FCSTD DOCUMENT  (FreeCAD 0.19R24291 (Git))
Label: 1U_erratic_radio_box_base
License: All rights reserved
LicenseURL: http://en.wikipedia.org/wiki/All_rights_reserved
objects: Part::Feature×29, App::Part×17, Sketcher::SketchObject×5, PartDesign::Pad×4, PartDesign::Body×2, Mesh::Feature×1, PartDesign::Pocket×1
note: 46 computed .brp shape members not serialized (recipe doc carries the construction recipe); baked Part::Feature solids carry a one-line shape summary decoded from their .brp

FEATURE [Sketcher::SketchObject] Sketch
  FullyConstrained = true
  MapMode = 5
  Support = -> [XY_Plane]
  sketch-geometry (44):
    g0: LineSegment StartX=200 StartY=123 StartZ=0 EndX=200 EndY=-123 EndZ=0
    g1: LineSegment StartX=200 StartY=-123 StartZ=0 EndX=-200 EndY=-123 EndZ=0
    g2: LineSegment StartX=-200 StartY=-123 StartZ=0 EndX=-200 EndY=123 EndZ=0
    g3: LineSegment StartX=200 StartY=-123 StartZ=0 EndX=200 EndY=-87 EndZ=0
    g4: LineSegment StartX=200 StartY=-87 StartZ=0 EndX=190 EndY=-87 EndZ=0
    g5: LineSegment StartX=190 StartY=-87 StartZ=0 EndX=190 EndY=-71 EndZ=0
    g6: LineSegment StartX=190 StartY=-71 StartZ=0 EndX=200 EndY=-71 EndZ=0
    g7: LineSegment StartX=200 StartY=-71 StartZ=0 EndX=200 EndY=0 EndZ=0
    g8: LineSegment StartX=-200 StartY=-123 StartZ=0 EndX=-200 EndY=-87 EndZ=0
    g9: LineSegment StartX=-200 StartY=-87 StartZ=0 EndX=-190 EndY=-87 EndZ=0
    g10: LineSegment StartX=-190 StartY=-87 StartZ=0 EndX=-190 EndY=-71 EndZ=0
    g11: LineSegment StartX=-190 StartY=-71 StartZ=0 EndX=-200 EndY=-71 EndZ=0
    g12: LineSegment StartX=-200 StartY=-71 StartZ=0 EndX=-200 EndY=0 EndZ=0
    g13: LineSegment StartX=-200 StartY=123 StartZ=0 EndX=-200 EndY=87 EndZ=0
    g14: LineSegment StartX=-200 StartY=87 StartZ=0 EndX=-190 EndY=87 EndZ=0
    g15: LineSegment StartX=-190 StartY=87 StartZ=0 EndX=-190 EndY=71 EndZ=0
    g16: LineSegment StartX=-190 StartY=71 StartZ=0 EndX=-200 EndY=71 EndZ=0
    g17: LineSegment StartX=-200 StartY=71 StartZ=0 EndX=-200 EndY=0 EndZ=0
    g18: LineSegment StartX=200 StartY=123 StartZ=0 EndX=200 EndY=87 EndZ=0
    g19: LineSegment StartX=200 StartY=87 StartZ=0 EndX=190 EndY=87 EndZ=0
    g20: LineSegment StartX=190 StartY=87 StartZ=0 EndX=190 EndY=71 EndZ=0
    g21: LineSegment StartX=190 StartY=71 StartZ=0 EndX=200 EndY=71 EndZ=0
    g22: LineSegment StartX=200 StartY=71 StartZ=0 EndX=200 EndY=0 EndZ=0
    g23: GeomPoint X=-160 Y=123 Z=0
    g24: GeomPoint X=0 Y=123 Z=0
    g25: GeomPoint X=160 Y=123 Z=0
    g26: LineSegment StartX=-160 StartY=123 StartZ=0 EndX=0 EndY=123 EndZ=0
    g27: LineSegment StartX=160 StartY=123 StartZ=0 EndX=0 EndY=123 EndZ=0
    g28: LineSegment StartX=-200 StartY=123 StartZ=0 EndX=-168 EndY=123 EndZ=0
    g29: LineSegment StartX=-168 StartY=123 StartZ=0 EndX=-168 EndY=113 EndZ=0
    g30: LineSegment StartX=-168 StartY=113 StartZ=0 EndX=-152 EndY=113 EndZ=0
    g31: LineSegment StartX=-152 StartY=113 StartZ=0 EndX=-152 EndY=123 EndZ=0
    g32: LineSegment StartX=-152 StartY=123 StartZ=0 EndX=-8 EndY=123 EndZ=0
    g33: LineSegment StartX=-8 StartY=123 StartZ=0 EndX=-8 EndY=113 EndZ=0
    g34: LineSegment StartX=-8 StartY=113 StartZ=0 EndX=8 EndY=113 EndZ=0
    g35: LineSegment StartX=8 StartY=113 StartZ=0 EndX=8 EndY=123 EndZ=0
    g36: LineSegment StartX=8 StartY=123 StartZ=0 EndX=152 EndY=123 EndZ=0
    g37: LineSegment StartX=152 StartY=123 StartZ=0 EndX=152 EndY=113 EndZ=0
    g38: LineSegment StartX=152 StartY=113 StartZ=0 EndX=168 EndY=113 EndZ=0
    g39: LineSegment StartX=168 StartY=113 StartZ=0 EndX=168 EndY=123 EndZ=0
    g40: LineSegment StartX=168 StartY=123 StartZ=0 EndX=200 EndY=123 EndZ=0
    g41: GeomPoint X=160 Y=113 Z=0
    g42: GeomPoint X=0 Y=113 Z=0
    g43: GeomPoint X=-160 Y=113 Z=0
  constraints (118):
    c: Coincident(g0,g1)
    c: Coincident(g1,g2)
    c: Horizontal(g1)
    c: Vertical(g0)
    c: Vertical(g2)
    c: Symmetric(g0,g1,g-1)
    c: DistanceX(g1,g1) = 400
    c: DistanceY(g0,g0) = 246
    c: Coincident(g3,g1)
    c: PointOnObject(g3,g0)
    c: Coincident(g4,g3)
    c: Horizontal(g4)
    c: Coincident(g5,g4)
    c: Vertical(g5)
    c: Coincident(g6,g5)
    c: PointOnObject(g6,g0)
    c: Horizontal(g6)
    c: Coincident(g7,g6)
    c: PointOnObject(g7,g0)
    c: PointOnObject(g7,g-1)
    c: DistanceY(g1,g3) = 36
    c: DistanceY(g1,g6) = 52
    c: DistanceX(g4,g4) = 10
    c: Coincident(g9,g8)
    c: Horizontal(g9)
    c: Coincident(g10,g9)
    c: Vertical(g10)
    c: Coincident(g11,g10)
    c: Horizontal(g11)
    c: Coincident(g12,g11)
    c: Coincident(g19,g18)
    c: Horizontal(g19)
    c: Coincident(g20,g19)
    c: Vertical(g20)
    c: Coincident(g21,g20)
    c: Horizontal(g21)
    c: Coincident(g22,g21)
    c: Coincident(g14,g13)
    c: Horizontal(g14)
    c: Coincident(g15,g14)
    c: Vertical(g15)
    c: Coincident(g16,g15)
    c: Horizontal(g16)
    c: Coincident(g17,g16)
    c: Equal(g5,g20)
    c: Equal(g20,g15)
    c: Equal(g15,g10)
    c: Equal(g21,g4)
    c: Equal(g4,g9)
    c: Equal(g9,g16)
    c: Equal(g3,g8)
    c: Equal(g8,g13)
    c: Equal(g13,g18)
    c: Coincident(g12,g17)
    c: PointOnObject(g12,g-1)
    c: PointOnObject(g12,g2)
    c: Vertical(g12)
    c: Coincident(g8,g1)
    c: Vertical(g8)
    c: Vertical(g17)
    c: Vertical(g13)
    c: Vertical(g22)
    c: Coincident(g7,g22)
    c: Vertical(g18)
    c: PointOnObject(g24,g-2)
    c: DistanceX(g24,g25) = 160
    c: Coincident(g26,g23)
    c: Coincident(g26,g24)
    c: Coincident(g27,g25)
    c: Coincident(g27,g24)
    c: Horizontal(g24,g18)
    c: Equal(g27,g26)
    c: Horizontal(g27)
    c: Horizontal(g26)
    c: Horizontal(g2,g18)
    c: Coincident(g13,g2)
    c: Coincident(g18,g0)
    c: Coincident(g13,g28)
    c: Horizontal(g28)
    c: Coincident(g28,g29)
    c: Vertical(g29)
    c: Coincident(g29,g30)
    c: Horizontal(g30)
    c: Coincident(g30,g31)
    c: PointOnObject(g31,g26)
    c: Vertical(g31)
    c: Horizontal(g32)
    c: Coincident(g32,g33)
    c: Vertical(g33)
    c: Coincident(g33,g34)
    c: Horizontal(g34)
    c: Coincident(g34,g35)
    c: PointOnObject(g35,g27)
    c: Vertical(g35)
    c: Coincident(g35,g36)
    c: PointOnObject(g36,g27)
    c: Coincident(g36,g37)
    c: Coincident(g37,g38)
    c: Horizontal(g38)
    c: Coincident(g38,g39)
    c: Vertical(g39)
    c: Coincident(g39,g40)
    c: Coincident(g40,g18)
    c: Vertical(g37)
    c: Equal(g38,g34)
    c: Equal(g34,g30)
    c: Equal(g30,g5)
    c: Horizontal(g40)
    c: Equal(g31,g35)
    c: Equal(g35,g39)
    c: Equal(g39,g21)
    c: Symmetric(g38,g37,g41)
    c: Vertical(g41,g25)
    c: Symmetric(g34,g33,g42)
    c: Vertical(g42,g24)
    c: Symmetric(g30,g29,g43)
    c: Vertical(g43,g23)
    c: Coincident(g32,g31)
FEATURE [PartDesign::Pad] Pad
  Direction = (1,1,1)
  Length = 5
  Length2 = 100
  Profile = -> Sketch
  Type = 0
FEATURE [Part::Feature] Part__Feature  label="p2"
  Placement = pos=(0,0,0.5) rot=(0,0,1;0rad)
  shape: bbox 62.5 x 51.1 x 28 mm, 628 faces (baked)
FEATURE [Part::Feature] Part__Feature001  label="PCB"
  Placement = pos=(-7.1e-15,0.2,0) rot=(0,0,1;0rad)
  shape: bbox 73.06 x 49 x 22.6 mm, 145 faces (baked)
FEATURE [App::Part] RS_15  label="RS-15 A"
  Group = -> [Part__Feature,Part__Feature001]
  Origin = -> Origin002
  Placement = pos=(-80,-61,34) rot=(0,0,1;1.5708rad)
FEATURE [Part::Feature] Part__Feature002  label="Raspberry Pi 3 Light Version"
  Placement = pos=(-103,69,11) rot=(0,0,1;0rad)
  shape: bbox 89.96 x 57.63 x 18.91 mm, 9075 faces, 217 solids (baked)
FEATURE [App::Part] Part001  label="RaspberryPi"
  Group = -> [Part__Feature002]
  Origin = -> Origin003
  Placement = pos=(5,9,0) rot=(0,0,1;0rad)
FEATURE [Part::Feature] Part__Feature003  label="PCB001"
  Placement = pos=(-7.1e-15,0.2,0) rot=(0,0,1;0rad)
  shape: bbox 73.06 x 49 x 22.6 mm, 145 faces (baked)
FEATURE [Part::Feature] Part__Feature004  label="p003"
  Placement = pos=(0,0,0.5) rot=(0,0,1;0rad)
  shape: bbox 62.5 x 51.1 x 28 mm, 628 faces (baked)
FEATURE [App::Part] RS_016  label="RS-15 B"
  Group = -> [Part__Feature004,Part__Feature003]
  Origin = -> Origin004
  Placement = pos=(-19,-61,34) rot=(0,0,1;1.5708rad)
FEATURE [Part::Feature] Part__Feature005  label="Pcb"
  Placement = pos=(-142.73,80.22,0) rot=(0,0,1;0rad)
  shape: bbox 55.31 x 70 x 1.6 mm, 52 faces (baked)
FEATURE [Part::Feature] Part__Feature006  label="PCB_Sketch"
  shape: bbox 55.31 x 70 x 2e-07 mm, 0 faces, 0 solids (baked)
FEATURE [App::Part] Board_Geoms
  Group = -> [Part__Feature005,Part__Feature006]
  Origin = -> Origin006
FEATURE [Part::Feature] Part__Feature007  label="C22_CP_Elec_5x53_58AF1F3F"
  Placement = pos=(-2.94,-32.29,0) rot=(0,0,1;3.14159rad)
  shape: bbox 6.985 x 6.828 x 5.3 mm, 41 faces (baked)
FEATURE [Part::Feature] Part__Feature008  label="C23_CP_Elec_5x53_58AF1F4D"
  Placement = pos=(-2.6,-14.04,0) rot=(0,0,1;3.14159rad)
  shape: bbox 6.985 x 6.828 x 5.3 mm, 41 faces (baked)
FEATURE [Part::Feature] Part__Feature009  label="C24_CP_Elec_5x53_58AF1F5B"
  Placement = pos=(-2.79,3.79,0) rot=(0,0,1;3.14159rad)
  shape: bbox 6.985 x 6.828 x 5.3 mm, 41 faces (baked)
FEATURE [Part::Feature] Part__Feature010  label="J1_676430910_58AF1F9A"
  Placement = pos=(2.25,-26.25,0) rot=(0.57735,0.57735,0.57735;2.0944rad)
  shape: bbox 15.26 x 16.01 x 11.45 mm, 499 faces (baked)
FEATURE [Part::Feature] Part__Feature011  label="J2_676430910_58AF1FA7"
  Placement = pos=(2.25,-8.15,0) rot=(0.57735,0.57735,0.57735;2.0944rad)
  shape: bbox 15.26 x 16.01 x 11.45 mm, 499 faces (baked)
FEATURE [Part::Feature] Part__Feature012  label="J3_676430910_58AF1FB4[2]"
  Placement = pos=(2.25,9.84,0) rot=(0.57735,0.57735,0.57735;2.0944rad)
  shape: bbox 15.26 x 16.01 x 11.45 mm, 499 faces (baked)
FEATURE [Part::Feature] Part__Feature013  label="P1_USB_Micro-B_Molex_47346-0001_58AF1FC6"
  Placement = pos=(-36.58,18.53,0) rot=(0,0,-1;1.5708rad)
  shape: bbox 5.418 x 7.977 x 2.937 mm, 484 faces (baked)
FEATURE [Part::Feature] Part__Feature014  label="P5_USB_Mini-B_Lumberg_2486_01_Horizontal_58AF1FEC"
  Placement = pos=(-34.75,-26.5,0) rot=(0,0,-1;1.5708rad)
  shape: bbox 9.2 x 9.9 x 4.997 mm, 472 faces (baked)
FEATURE [App::Part] Top
  Group = -> [Part__Feature007,Part__Feature008,Part__Feature009,Part__Feature010,Part__Feature011,Part__Feature012,Part__Feature013,Part__Feature014]
  Origin = -> Origin007
FEATURE [App::Part] Step_Models
  Group = -> [Top]
  Origin = -> Origin008
FEATURE [App::Part] YKUSH  label="YKUSH_A"
  Group = -> [Board_Geoms,Step_Models]
  Origin = -> Origin009
  Placement = pos=(0,-69,10) rot=(0,0,1;0rad)
FEATURE [App::Part] Part003  label="SMPS"
  Group = -> [RS_016,RS_15]
  Origin = -> Origin010
  Placement = pos=(-1,-8,0) rot=(0,0,1;0rad)
FEATURE [Part::Feature] Part__Feature015  label="C23_CP_Elec_5x53_58AF1F4D001"
  Placement = pos=(-2.6,-14.04,0) rot=(0,0,1;3.14159rad)
  shape: bbox 6.985 x 6.828 x 5.3 mm, 41 faces (baked)
FEATURE [Part::Feature] Part__Feature016  label="J1_676430910_58AF1F9A001"
  Placement = pos=(2.25,-26.25,0) rot=(0.57735,0.57735,0.57735;2.0944rad)
  shape: bbox 15.26 x 16.01 x 11.45 mm, 499 faces (baked)
FEATURE [Part::Feature] Part__Feature017  label="Pcb001"
  Placement = pos=(-142.73,80.22,0) rot=(0,0,1;0rad)
  shape: bbox 55.31 x 70 x 1.6 mm, 52 faces (baked)
FEATURE [Part::Feature] Part__Feature018  label="C24_CP_Elec_5x53_58AF1F5B001"
  Placement = pos=(-2.79,3.79,0) rot=(0,0,1;3.14159rad)
  shape: bbox 6.985 x 6.828 x 5.3 mm, 41 faces (baked)
FEATURE [Part::Feature] Part__Feature019  label="J2_676430910_58AF1FA008"
  Placement = pos=(2.25,-8.15,0) rot=(0.57735,0.57735,0.57735;2.0944rad)
  shape: bbox 15.26 x 16.01 x 11.45 mm, 499 faces (baked)
FEATURE [Part::Feature] Part__Feature020  label="J3_676430910_58AF1FB4[2]001"
  Placement = pos=(2.25,9.84,0) rot=(0.57735,0.57735,0.57735;2.0944rad)
  shape: bbox 15.26 x 16.01 x 11.45 mm, 499 faces (baked)
FEATURE [Part::Feature] Part__Feature021  label="PCB_Sketch001"
  shape: bbox 55.31 x 70 x 2e-07 mm, 0 faces, 0 solids (baked)
FEATURE [App::Part] Board_Geoms001
  Group = -> [Part__Feature017,Part__Feature021]
  Origin = -> Origin012
FEATURE [Part::Feature] Part__Feature022  label="P1_USB_Micro-B_Molex_47346-0001_58AF1FC007"
  Placement = pos=(-36.58,18.53,0) rot=(0,0,-1;1.5708rad)
  shape: bbox 5.418 x 7.977 x 2.937 mm, 484 faces (baked)
FEATURE [Part::Feature] Part__Feature023  label="P5_USB_Mini-B_Lumberg_2486_01_Horizontal_58AF1FEC001"
  Placement = pos=(-34.75,-26.5,0) rot=(0,0,-1;1.5708rad)
  shape: bbox 9.2 x 9.9 x 4.997 mm, 472 faces (baked)
FEATURE [Part::Feature] Part__Feature024  label="C22_CP_Elec_5x53_58AF1F3F001"
  Placement = pos=(-2.94,-32.29,0) rot=(0,0,1;3.14159rad)
  shape: bbox 6.985 x 6.828 x 5.3 mm, 41 faces (baked)
FEATURE [App::Part] Top001
  Group = -> [Part__Feature024,Part__Feature015,Part__Feature018,Part__Feature016,Part__Feature019,Part__Feature020,Part__Feature022,Part__Feature023]
  Origin = -> Origin011
FEATURE [App::Part] Step_Models001
  Group = -> [Top001]
  Origin = -> Origin013
FEATURE [App::Part] YKUSH001  label="YKUSH_B"
  Group = -> [Board_Geoms001,Step_Models001]
  Origin = -> Origin014
  Placement = pos=(0,-69,24) rot=(0,0,1;0rad)
FEATURE [App::Part] Part002  label="Ykushes"
  Group = -> [YKUSH,YKUSH001]
  Origin = -> Origin005
  Placement = pos=(-0.6,4.5,0) rot=(0,0,1;0rad)
FEATURE [Mesh::Feature] HackRF_One
  Placement = pos=(164,105.3,8) rot=(0,0,1;3.14159rad)
FEATURE [Sketcher::SketchObject] Sketch001
  FullyConstrained = true
  MapMode = 5
  Support = -> [XY_Plane016]
  sketch-geometry (4):
    g0: LineSegment StartX=-26.5 StartY=20 StartZ=0 EndX=26.5 EndY=20 EndZ=0
    g1: LineSegment StartX=26.5 StartY=20 StartZ=0 EndX=26.5 EndY=-20 EndZ=0
    g2: LineSegment StartX=26.5 StartY=-20 StartZ=0 EndX=-26.5 EndY=-20 EndZ=0
    g3: LineSegment StartX=-26.5 StartY=-20 StartZ=0 EndX=-26.5 EndY=20 EndZ=0
  constraints (11):
    c: Coincident(g0,g1)
    c: Coincident(g1,g2)
    c: Coincident(g2,g3)
    c: Coincident(g3,g0)
    c: Horizontal(g0)
    c: Horizontal(g2)
    c: Vertical(g1)
    c: Vertical(g3)
    c: Symmetric(g0,g2,g-1)
    c: DistanceX(g2,g2) = 53
    c: DistanceY(g1,g1) = 40
FEATURE [PartDesign::Pad] Pad001
  Direction = (1,1,1)
  Length = 25
  Length2 = 100
  Profile = -> Sketch001
  Type = 0
FEATURE [Sketcher::SketchObject] Sketch002
  FullyConstrained = true
  MapMode = 5
  Placement = pos=(26.5,0,0) rot=(0.57735,0.57735,0.57735;2.0944rad)
  Support = -> [Pad001]
  sketch-geometry (1):
    g0: Circle CenterX=0 CenterY=13 CenterZ=0 NormalX=0 NormalY=0 NormalZ=1 AngleXU=0 Radius=5
  constraints (3):
    c: PointOnObject(g0,g-2)
    c: Diameter(g0) = 10
    c: DistanceY(g-1,g0) = 13
FEATURE [PartDesign::Pad] Pad002
  BaseFeature = -> Pad001
  Direction = (1,1,1)
  Length = 10
  Length2 = 100
  Profile = -> Sketch002
  Type = 0
FEATURE [Sketcher::SketchObject] Sketch003
  ExternalGeometry = -> [Pad002]
  FullyConstrained = true
  MapMode = 5
  Placement = pos=(-26.5,0,0) rot=(0.57735,-0.57735,-0.57735;2.0944rad)
  Support = -> [Pad002]
  sketch-geometry (6):
    g0: Circle CenterX=-5.5 CenterY=10 CenterZ=0 NormalX=0 NormalY=0 NormalZ=1 AngleXU=0 Radius=2.5
    g1: LineSegment StartX=-1.5 StartY=12.5 StartZ=0 EndX=9.5 EndY=12.5 EndZ=0
    g2: LineSegment StartX=9.5 StartY=12.5 StartZ=0 EndX=9.5 EndY=5.5 EndZ=0
    g3: LineSegment StartX=9.5 StartY=5.5 StartZ=0 EndX=-1.5 EndY=5.5 EndZ=0
    g4: LineSegment StartX=-1.5 StartY=5.5 StartZ=0 EndX=-1.5 EndY=12.5 EndZ=0
    g5: GeomPoint X=4 Y=9 Z=0
  constraints (16):
    c: Coincident(g1,g2)
    c: Coincident(g2,g3)
    c: Coincident(g3,g4)
    c: Coincident(g4,g1)
    c: Horizontal(g1)
    c: Horizontal(g3)
    c: Vertical(g2)
    c: Vertical(g4)
    c: Diameter(g0) = 5
    c: DistanceY(g-1,g0) = 10
    c: DistanceX(g-3,g0) = 14.5
    c: Symmetric(g1,g3,g5)
    c: DistanceY(g-1,g5) = 9
    c: DistanceY(g2,g2) = 7
    c: DistanceX(g1,g1) = 11
    c: DistanceX(g-3,g5) = 24
FEATURE [PartDesign::Pad] Pad003
  BaseFeature = -> Pad002
  Direction = (1,1,1)
  Length = 10
  Length2 = 100
  Profile = -> Sketch003
  Type = 0
FEATURE [PartDesign::Body] Body001
  Group = -> [Sketch001,Pad001,Sketch002,Pad002,Sketch003,Pad003]
  Origin = -> Origin016
  Placement = pos=(0,0,6) rot=(0,0,1;0rad)
  Tip = -> Pad003
FEATURE [App::Part] Part004  label="AIRSPY mock"
  Group = -> [Body001]
  Origin = -> Origin015
  Placement = pos=(15.5,-4,1.1) rot=(0,0,1;0rad)
FEATURE [Sketcher::SketchObject] Sketch004
  FullyConstrained = false
  MapMode = 5
  Placement = pos=(0,0,5) rot=(0,0,1;0rad)
  Support = -> [Pad]
  sketch-geometry (44):
    g0: LineSegment StartX=-180 StartY=105 StartZ=0 EndX=180 EndY=105 EndZ=0
    g1: LineSegment StartX=180 StartY=105 StartZ=0 EndX=180 EndY=-105 EndZ=0
    g2: LineSegment StartX=180 StartY=-105 StartZ=0 EndX=-180 EndY=-105 EndZ=0
    g3: LineSegment StartX=-180 StartY=-105 StartZ=0 EndX=-180 EndY=105 EndZ=0
    g4: Circle CenterX=-180 CenterY=105 CenterZ=0 NormalX=0 NormalY=0 NormalZ=1 AngleXU=0 Radius=1.6
    g5: Circle CenterX=-180 CenterY=-105 CenterZ=0 NormalX=0 NormalY=0 NormalZ=1 AngleXU=0 Radius=1.6
    g6: Circle CenterX=180 CenterY=-105 CenterZ=0 NormalX=0 NormalY=0 NormalZ=1 AngleXU=0 Radius=1.6
    g7: Circle CenterX=180 CenterY=105 CenterZ=0 NormalX=0 NormalY=0 NormalZ=1 AngleXU=0 Radius=1.6
    g8: Circle CenterX=-90 CenterY=-5 CenterZ=0 NormalX=0 NormalY=0 NormalZ=1 AngleXU=0 Radius=1.6
    g9: Circle CenterX=-90 CenterY=-44 CenterZ=0 NormalX=0 NormalY=0 NormalZ=1 AngleXU=0 Radius=1.6
    g10: Circle CenterX=-152 CenterY=-5 CenterZ=0 NormalX=0 NormalY=0 NormalZ=1 AngleXU=0 Radius=1.6
    g11: Circle CenterX=-152 CenterY=-44 CenterZ=0 NormalX=0 NormalY=0 NormalZ=1 AngleXU=0 Radius=1.6
    g12: LineSegment StartX=-90 StartY=-5 StartZ=0 EndX=-152 EndY=-5 EndZ=0
    g13: Circle CenterX=-90 CenterY=-15 CenterZ=0 NormalX=0 NormalY=0 NormalZ=1 AngleXU=0 Radius=1.6
    g14: Circle CenterX=-90 CenterY=-54 CenterZ=0 NormalX=0 NormalY=0 NormalZ=1 AngleXU=0 Radius=1.6
    g15: Circle CenterX=-152 CenterY=-15 CenterZ=0 NormalX=0 NormalY=0 NormalZ=1 AngleXU=0 Radius=1.6
    g16: Circle CenterX=-152 CenterY=-54 CenterZ=0 NormalX=0 NormalY=0 NormalZ=1 AngleXU=0 Radius=1.6
    g17: LineSegment StartX=-90 StartY=-15 StartZ=0 EndX=-152 EndY=-15 EndZ=0
    g18: LineSegment StartX=-90 StartY=-5 StartZ=0 EndX=-90 EndY=-15 EndZ=0
    g19: Circle CenterX=-90 CenterY=-25 CenterZ=0 NormalX=0 NormalY=0 NormalZ=1 AngleXU=0 Radius=1.6
    g20: Circle CenterX=-90 CenterY=-64 CenterZ=0 NormalX=0 NormalY=0 NormalZ=1 AngleXU=0 Radius=1.6
    g21: Circle CenterX=-152 CenterY=-25 CenterZ=0 NormalX=0 NormalY=0 NormalZ=1 AngleXU=0 Radius=1.6
    g22: Circle CenterX=-152 CenterY=-64 CenterZ=0 NormalX=0 NormalY=0 NormalZ=1 AngleXU=0 Radius=1.6
    g23: LineSegment StartX=-90 StartY=-25 StartZ=0 EndX=-152 EndY=-25 EndZ=0
    g24: LineSegment StartX=-90 StartY=-15 StartZ=0 EndX=-90 EndY=-25 EndZ=0
    g25: LineSegment StartX=-143 StartY=56 StartZ=0 EndX=-85 EndY=56 EndZ=0
    g26: LineSegment StartX=-85 StartY=56 StartZ=0 EndX=-85 EndY=105 EndZ=0
    g27: LineSegment StartX=-85 StartY=105 StartZ=0 EndX=-143 EndY=105 EndZ=0
    g28: LineSegment StartX=-143 StartY=105 StartZ=0 EndX=-143 EndY=56 EndZ=0
    g29: Circle CenterX=-143 CenterY=105 CenterZ=0 NormalX=0 NormalY=0 NormalZ=1 AngleXU=0 Radius=1.6
    g30: Circle CenterX=-143 CenterY=56 CenterZ=0 NormalX=0 NormalY=0 NormalZ=1 AngleXU=0 Radius=1.6
    g31: Circle CenterX=-85 CenterY=56 CenterZ=0 NormalX=0 NormalY=0 NormalZ=1 AngleXU=0 Radius=1.6
    g32: Circle CenterX=-85 CenterY=105 CenterZ=0 NormalX=0 NormalY=0 NormalZ=1 AngleXU=0 Radius=1.6
    g33: LineSegment StartX=-37.91 StartY=-38 StartZ=0 EndX=12 EndY=-38 EndZ=0
    g34: LineSegment StartX=12 StartY=-38 StartZ=0 EndX=12 EndY=-102.69 EndZ=0
    g35: LineSegment StartX=12 StartY=-102.69 StartZ=0 EndX=-37.91 EndY=-102.69 EndZ=0
    g36: LineSegment StartX=-37.91 StartY=-102.69 StartZ=0 EndX=-37.91 EndY=-38 EndZ=0
    g37: Circle CenterX=-37.91 CenterY=-38 CenterZ=0 NormalX=0 NormalY=0 NormalZ=1 AngleXU=0 Radius=1.6
    g38: Circle CenterX=12 CenterY=-38 CenterZ=0 NormalX=0 NormalY=0 NormalZ=1 AngleXU=0 Radius=1.6
    g39: Circle CenterX=-37.91 CenterY=-102.69 CenterZ=0 NormalX=0 NormalY=0 NormalZ=1 AngleXU=0 Radius=1.6
    g40: Circle CenterX=12 CenterY=-102.69 CenterZ=0 NormalX=0 NormalY=0 NormalZ=1 AngleXU=0 Radius=1.6
    g41: LineSegment StartX=-55 StartY=0 StartZ=0 EndX=55 EndY=0 EndZ=0
    g42: Circle CenterX=-55 CenterY=0 CenterZ=0 NormalX=0 NormalY=0 NormalZ=1 AngleXU=0 Radius=1.6
    g43: Circle CenterX=55 CenterY=0 CenterZ=0 NormalX=0 NormalY=0 NormalZ=1 AngleXU=0 Radius=1.6
  constraints (102):
    c: Coincident(g0,g1)
    c: Coincident(g1,g2)
    c: Coincident(g2,g3)
    c: Coincident(g3,g0)
    c: Horizontal(g0)
    c: Horizontal(g2)
    c: Vertical(g1)
    c: Vertical(g3)
    c: Symmetric(g0,g2,g-1)
    c: DistanceY(g1,g1) = 210
    c: DistanceX(g0,g0) = 360
    c: Coincident(g4,g0)
    c: Diameter(g4) = 3.2
    c: Equal(g4,g5) = 3.2
    c: Coincident(g5,g2)
    c: Equal(g4,g6) = 3.2
    c: Coincident(g6,g1)
    c: Equal(g4,g7) = 3.2
    c: Coincident(g7,g0)
    c: Equal(g4,g8) = 3.2
    c: Equal(g4,g9) = 3.2
    c: Vertical(g8,g9)
    c: DistanceY(g9,g8) = 39
    c: DistanceY(g8,g-1) = 5
    c: Vertical(g10,g11)
    c: DistanceY(g11,g10) = 39
    c: Coincident(g8,g12)
    c: Coincident(g10,g12)
    c: Horizontal(g12)
    c: DistanceX(g8,g-1) = 90
    c: DistanceX(g12,g12) = 62
    c: Vertical(g13,g14)
    c: DistanceY(g14,g13) = 39
    c: Vertical(g15,g16)
    c: DistanceY(g16,g15) = 39
    c: Coincident(g13,g17)
    c: Coincident(g15,g17)
    c: Horizontal(g17)
    c: Equal(g12,g17) = 62
    c: Coincident(g8,g18)
    c: Coincident(g13,g18)
    c: Distance(g18) = 10
    c: Vertical(g19,g20)
    c: DistanceY(g20,g19) = 39
    c: Vertical(g21,g22)
    c: DistanceY(g22,g21) = 39
    c: Coincident(g19,g23)
    c: Coincident(g21,g23)
    c: Horizontal(g23)
    c: Equal(g12,g23) = 62
    c: Coincident(g13,g24)
    c: Coincident(g19,g24)
    c: Equal(g18,g24)
    c: Parallel(g24,g18)
    c: Vertical(g18)
    c: Coincident(g25,g26)
    c: Coincident(g26,g27)
    c: Coincident(g27,g28)
    c: Coincident(g28,g25)
    c: Horizontal(g25)
    c: Horizontal(g27)
    c: Vertical(g26)
    c: Vertical(g28)
    c: DistanceX(g27,g27) = 58
    c: DistanceY(g28,g28) = 49
    c: DistanceX(g26,g-1) = 85
    c: DistanceY(g-1,g26) = 105
    c: Equal(g4,g29) = 3.2
    c: Coincident(g29,g27)
    c: Equal(g4,g30) = 3.2
    c: Coincident(g30,g25)
    c: Equal(g4,g31) = 3.2
    c: Coincident(g31,g25)
    c: Equal(g4,g32) = 3.2
    c: Coincident(g32,g26)
    c: Coincident(g33,g34)
    c: Coincident(g34,g35)
    c: Coincident(g35,g36)
    c: Coincident(g36,g33)
    c: Horizontal(g33)
    c: Horizontal(g35)
    c: Vertical(g34)
    c: Vertical(g36)
    c: DistanceX(g33,g33) = 49.91
    c: DistanceY(g34,g34) = 64.69
    c: Equal(g4,g37) = 3.2
    c: Coincident(g37,g33)
    c: Equal(g4,g38) = 3.2
    c: Coincident(g38,g33)
    c: Equal(g4,g39) = 3.2
    c: Coincident(g39,g35)
    c: Equal(g4,g40) = 3.2
    c: Coincident(g40,g34)
    c: DistanceX(g-1,g38) = 12
    c: DistanceY(g38,g-1) = 38
    c: PointOnObject(g41,g-1)
    c: Symmetric(g41,g41,g-1)
    c: DistanceX(g41,g41) = 110
    c: Equal(g4,g42) = 3.2
    c: Coincident(g42,g41)
    c: Equal(g4,g43) = 3.2
    c: Coincident(g43,g41)
FEATURE [PartDesign::Pocket] Pocket
  BaseFeature = -> Pad
  Length = 5
  Length2 = 100
  Profile = -> Sketch004
  Type = 1
FEATURE [PartDesign::Body] Body
  Group = -> [Sketch,Pad,Sketch004,Pocket]
  Origin = -> Origin
  Tip = -> Pocket
FEATURE [App::Part] Part
  Group = -> [Body]
  Origin = -> Origin001
FEATURE [Part::Feature] Part__Feature025  label="Body_base"
  shape: bbox 87.2 x 47.2 x 27 mm, 84 faces (baked)
FEATURE [Part::Feature] Part__Feature026  label="Body_lid"
  Placement = pos=(0,0,25) rot=(0,0,1;0rad)
  shape: bbox 72 x 44.6 x 2 mm, 48 faces (baked)
FEATURE [App::Part] HackRF_One_holder
  Group = -> [Part__Feature025,Part__Feature026]
  Origin = -> Origin017
  Placement = pos=(15.4,-4,7) rot=(0,0,1;0rad)
FEATURE [Part::Feature] Part__Feature027  label="Body_base001"
  shape: bbox 157.2 x 87.2 x 21 mm, 84 faces (baked)
FEATURE [Part::Feature] Part__Feature028  label="Body_lid001"
  Placement = pos=(0,0,19) rot=(0,0,1;0rad)
  shape: bbox 142 x 83.6 x 2 mm, 48 faces (baked)
FEATURE [App::Part] HackRF_One_holder001
  Group = -> [Part__Feature027,Part__Feature028]
  Origin = -> Origin018
  Placement = pos=(93.3,67.9,6.9) rot=(0,0,1;0rad)
